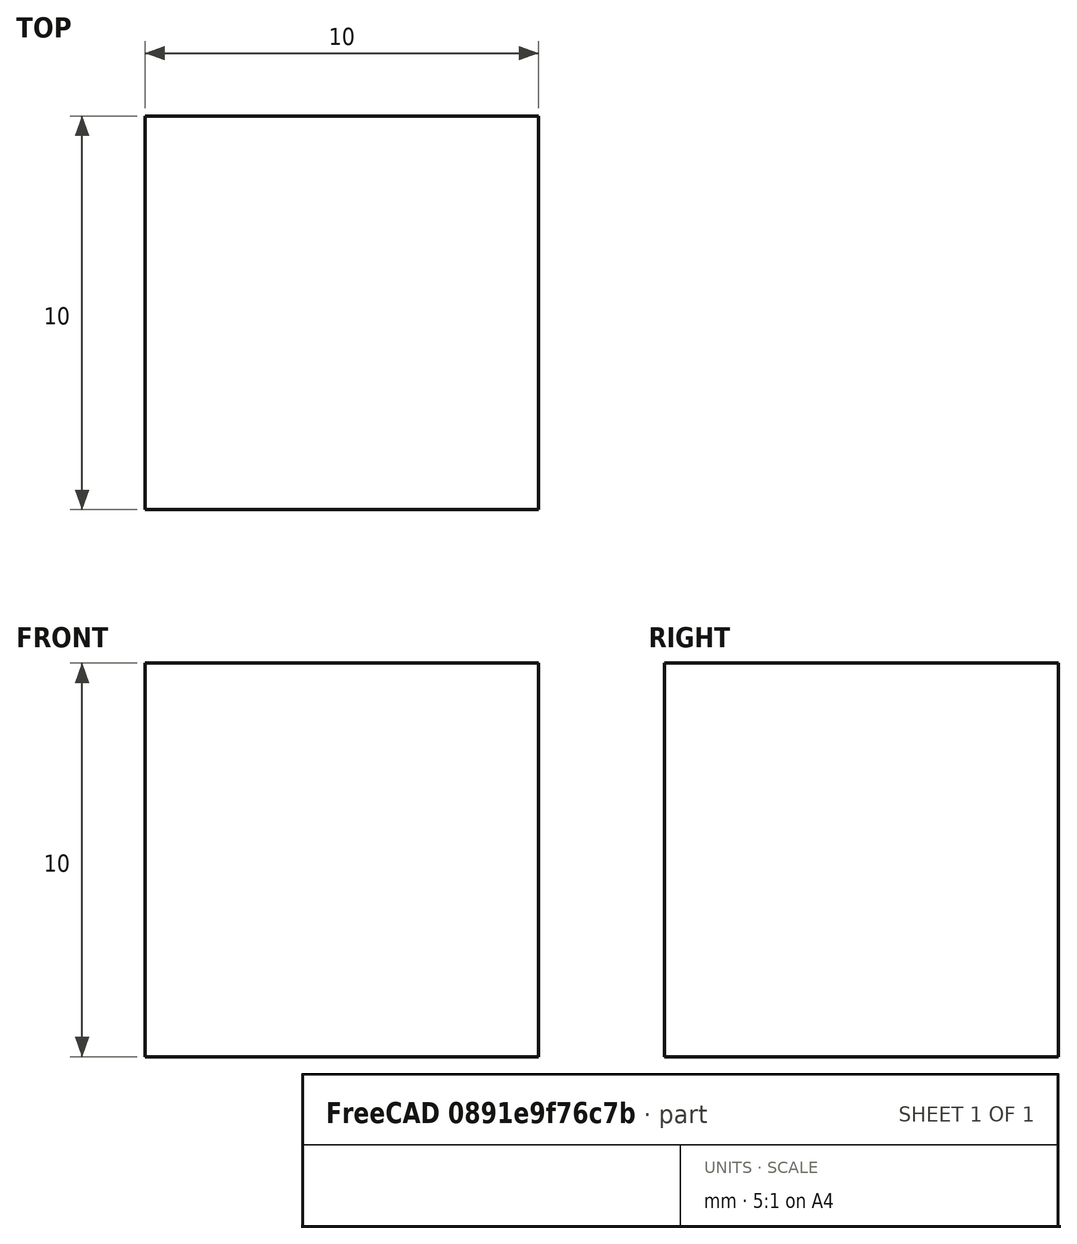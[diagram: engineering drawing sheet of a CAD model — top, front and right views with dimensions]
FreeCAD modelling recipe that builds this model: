
FCSTD DOCUMENT  (FreeCAD 1.0R39319 (Git))
Label: Box
License: All rights reserved
LicenseURL: https://en.wikipedia.org/wiki/All_rights_reserved
objects: Part::Box×1, App::FeaturePython×1
note: 1 computed .brp shape members not serialized (recipe doc carries the construction recipe); baked Part::Feature solids carry a one-line shape summary decoded from their .brp

FEATURE [Part::Box] Box  label="Cube"
  AttacherType = Attacher::AttachEngine3D
  Height = 10
  Length = 10
  Width = 10
FEATURE [App::FeaturePython] CLParamHub  # WARN: FeaturePython — macro-defined, semantics opaque (R4)
  LastPushJSON = {\n  "docName": "Box",\n  "docFile": "<userpath>/AppData/Roaming/FreeCAD/Mod/CalcsLiveWorkbench/models/Box.FCStd",\n  "params": [\n    {\n      "name": "Box/Length",\n      "label": "L",\n      "role": "both",\n      "pqKind": "Length",\n      "error": "'Base.Quantity' object has no attribute 'getUserPreferredUnit'"\n    },\n    {\n      "name": "Box/Width",\n      "label": "W",\n      "role": "both",\n      "pqKind": "Length",\n      "error": "'Base.Quantity' object has no attribute 'getUserPreferredUnit'"\n    },\n    {\n      "name": "Box/Height",\n      "label": "H",\n      "role": "both",\n      "pqKind": "Length",\n      "error": "'Base.Quantity' object has no attribute 'getUserPreferredUnit'"\n    }\n  ]\n}
  MappingJSON = {\n  "docVersion": "0.1",\n  "unitsSchema": "UserPreferred",\n  "params": [\n    {\n      "id": "Box.Length",\n      "label": "Length",\n      "path": "Box/Length",\n      "role": "both",\n      "pq": {\n        "kind": "Length",\n        "displayUnit": null\n      },\n      "notes": ""\n    },\n    {\n      "id": "Box.Width",\n      "label": "Width",\n      "path": "Box/Width",\n      "role": "both",\n      "pq": {\n        "kind": "Length",\n        "displayUnit": null\n      },\n      "notes": ""\n    },\n    {\n      "id": "Box.Height",\n      "label": "H",\n      "path": "Box/Height",\n      "role": "both",\n      "pq": {\n        "kind": "Length",\n        "displayUnit": "mm"\n      },\n      "notes": ""\n    }\n  ]\n}
